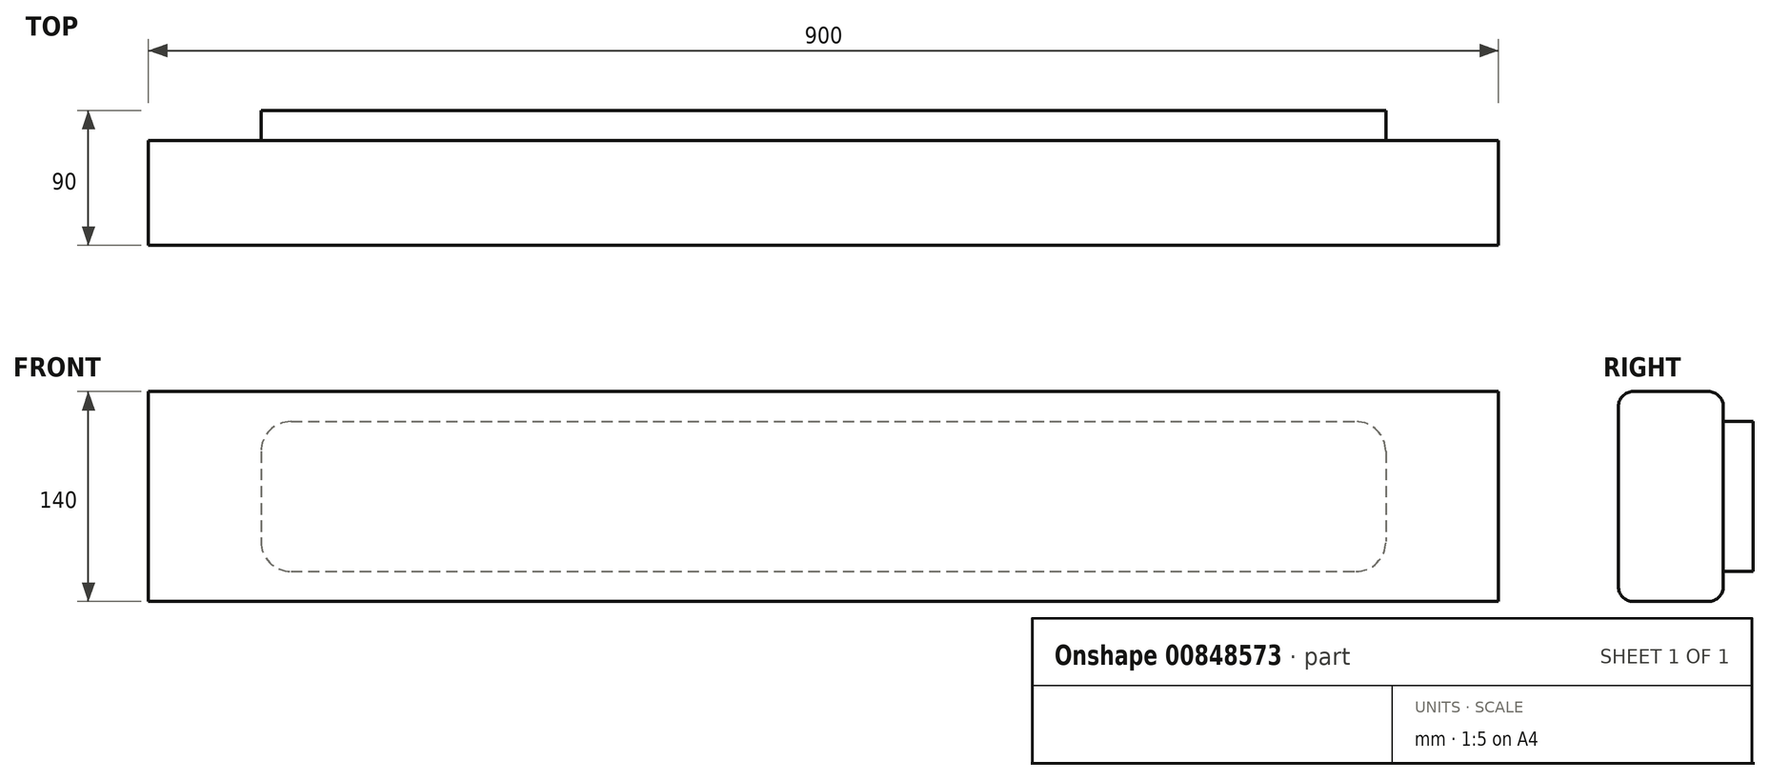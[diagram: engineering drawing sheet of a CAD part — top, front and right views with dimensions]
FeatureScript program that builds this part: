
annotation { "Feature Type Name" : "Feature", "Feature Type Description" : "" }
export const myFeature = defineFeature(function(context is Context, id is Id, definition is map)
    precondition{}
    {
        {
            var Q0;
            Q0=qCreatedBy(makeId("Front.planeOp"),FACE);
            var sketch = newSketch(context, id + "F0", { "sketchPlane" : qUnion([Q0])});
            skLineSegment(sketch, "E0.bottom", {"start": v(450, 70) * mm, "end": v(-450, 70) * mm});
            skLineSegment(sketch, "E0.top", {"start": v(450, -70) * mm, "end": v(-450, -70) * mm});
            skLineSegment(sketch, "E0.left", {"start": v(450, 70) * mm, "end": v(450, -70) * mm});
            skLineSegment(sketch, "E0.right", {"start": v(-450, 70) * mm, "end": v(-450, -70) * mm});
            skPoint(sketch, "E0.middle", {"position": v(0, 0) * mm});
            skSolve(sketch);
        }
        {
            var Q0;
            Q0 = qSketchRegion(id + "F0", true);
            extrude(context, id + "F1", {"entities" : qUnion([Q0]), "depth" : 70 * mm, "offsetDistance" : 25 * mm});
        }
        {
            var Q0;
            Q0=makeQuery(id+"F1.opExtrude","CAP_EDGE",EDGE,{"disambiguationData":[OSD([sQuery(id+"F0.wireOp",EDGE,"E0.bottom")])],"isStart":false});
            var Q1;
            Q1=makeQuery(id+"F1.opExtrude","CAP_EDGE",EDGE,{"disambiguationData":[OSD([sQuery(id+"F0.wireOp",EDGE,"E0.bottom")])],"isStart":true});
            var Q2;
            Q2=makeQuery(id+"F1.opExtrude","CAP_EDGE",EDGE,{"disambiguationData":[OSD([sQuery(id+"F0.wireOp",EDGE,"E0.top")])],"isStart":false});
            var Q3;
            Q3=makeQuery(id+"F1.opExtrude","CAP_EDGE",EDGE,{"disambiguationData":[OSD([sQuery(id+"F0.wireOp",EDGE,"E0.top")])],"isStart":true});
            fillet(context, id + "F2", {"entities" : qUnion([Q0, Q1, Q2, Q3]), "radius" : 10 * mm, "tangentPropagation" : true, "allowEdgeOverflow" : false});
        }
        {
            var Q0;
            Q0=makeQuery(id+"F1.opExtrude","CAP_FACE",FACE,{"disambiguationData":[OSD([sQuery(id+"F0.wireOp",EDGE,"E0.bottom"),sQuery(id+"F0.wireOp",EDGE,"E0.top"),sQuery(id+"F0.wireOp",EDGE,"E0.left"),sQuery(id+"F0.wireOp",EDGE,"E0.right")])],"isStart":true});
            var sketch = newSketch(context, id + "F3", { "sketchPlane" : qUnion([Q0])});
            skLineSegment(sketch, "E1.bottom", {"start": v(355, 50) * mm, "end": v(-355, 50) * mm});
            skLineSegment(sketch, "E1.top", {"start": v(355, -50) * mm, "end": v(-355, -50) * mm});
            skLineSegment(sketch, "E1.left", {"start": v(375, 30) * mm, "end": v(375, -30) * mm});
            skLineSegment(sketch, "E1.right", {"start": v(-375, 30) * mm, "end": v(-375, -30) * mm});
            skPoint(sketch, "E1.middle", {"position": v(0, 0) * mm});
            skPoint(sketch, "E2.visualSharp", {"position": v(-375, 50) * mm});
            skArc(sketch, "E2.filletArc", {"start": v(-355, 50) * mm, "mid": v(-369.14, 44.14) * mm, "end": v(-375, 30) * mm});
            skPoint(sketch, "E3.visualSharp", {"position": v(375, 50) * mm});
            skArc(sketch, "E3.filletArc", {"start": v(375, 30) * mm, "mid": v(369.14, 44.14) * mm, "end": v(355, 50) * mm});
            skPoint(sketch, "E4.visualSharp", {"position": v(375, -50) * mm});
            skArc(sketch, "E4.filletArc", {"start": v(355, -50) * mm, "mid": v(369.14, -44.14) * mm, "end": v(375, -30) * mm});
            skPoint(sketch, "E5.visualSharp", {"position": v(-375, -50) * mm});
            skArc(sketch, "E5.filletArc", {"start": v(-375, -30) * mm, "mid": v(-369.14, -44.14) * mm, "end": v(-355, -50) * mm});
            skSolve(sketch);
        }
        {
            var Q0;
            Q0 = qSketchRegion(id + "F3", true);
            extrude(context, id + "F4", {"entities" : qUnion([Q0]), "operationType" : NewBodyOperationType.ADD, "depth" : 20 * mm, "offsetDistance" : 25 * mm});
        }
    });
